# Revit family: Plumbing-Flushometer-Sloan-Valve-ROYAL-115-ESS_
name_source: partatom
category: Plumbing Fixtures
units: mm (PartAtom-declared; Revit-internal decimal feet)

## family parameters
Cut with Voids When Loaded = No
Host = Face
OmniClass Number = 23.45.05.14.99
OmniClass Title = Other Sanitary Washing Plumbing Fixtures
Part Type = Normal
Room Calculation Point = No
Round Connector Dimension = Use Diameter
Shared = No

## types (7) — shared parameters
Apparent Load = 0 VA
Assembly Code = D2020300
CW Connection = Yes
Centerline of Supply from Top of Fixture = 24"
Centerline of Supply to Centerline of Valve = 4 3/4"
Connector Description = Electrical Connection
Current = 0 A
Default Elevation = 0"
Edition number = 1
HW Connection = No
Height = 26 1/2"
Keynote = 15410
Manufacturer = Sloan Valve
Number of Poles = 1
Operating Water Pressure = 15 – 80 PSI (103 – 552 kPa)
Power Factor = 1
Product Material = Sloan Valve - Finish - Polished Chrome
Product data url = https://bimobject.com
URL = www.sloanvalve.com
Valve Pressure Drop = 0.00 psi
Vent Connection = No
Voltage = 24 V
Waste Connection = No
Water Inlet Connection Description = Water Inlet Connection
Water Inlet Connection Diameter = 1"
zero-valued in all types: CWFU, HWFU, WFU

## per-type parameters (varying)
| type | Description | Flush Rate | Part Number | z_2D_2 | z_Distance | z_No OFST | z_OFST | z_Offset | z_Pipe Offset |
| ROYAL 115 ESS-1.6-TMO-HW | 1.6 gpf, Polished Chrome Finish, Fixture Connection Top Spud, Single Flush, True Mechanical Override, Hardwired, Sensor-Operated, Royal® Exposed Sensor Hardwired Water Closet Flushometer. | 1.6 gpf (6.0 Lpf) | 3450310 | No | 2 1/4" | Yes | No | 2 1/4" | 1" |
| ROYAL 115 ESS-1.6-OR-2-OFST-HW | 1.6 gpf, Polished Chrome Finish, Fixture Connection Top Spud, Single Flush, 2 Offset, Electrical Override, Hardwired, Sensor-Operated, Royal® Exposed Sensor Hardwired Water Closet Flushometer. | 1.6 gpf (6.0 Lpf) | 3450348 | Yes | 1 1/4" | No | Yes | 3 1/4" | 2" |
| ROYAL 115 ESS-1.28-TMO-HW | 1.28 gpf, Polished Chrome Finish, Fixture Connection Top Spud, Single Flush, True Mechanical Override, Hardwired, Sensor-Operated, Royal® Exposed Sensor Hardwired Water Closet Flushometer. | 1.28 gpf (4.8 Lpf) | 3450312 | No | 2 1/4" | Yes | No | 2 1/4" | 1" |
| ROYAL 115 ESS-1.6-B-OR-HW | 1.6 gpf, Polished Chrome Finish, Fixture Connection Top Spud, Single Flush, Back of Valve Inlet, Electrical Override, Hardwired, SensorOperated, Royal® Exposed Sensor Hardwired Water Closet Flushometer. | 1.6 gpf (6.0 Lpf) | 3450349 | No | 2 1/4" | Yes | No | 2 1/4" | 1" |
| ROYAL 115 ESS-1.28-OR-HW | 1.28 gpf, Polished Chrome Finish, Fixture Connection Top Spud, Single Flush, Electrical Override, Hardwired, Sensor-Operated, Royal® Exposed Sensor Hardwired Water Closet Flushometer. | 1.28 gpf (4.8 Lpf) | 3450351 | No | 2 1/4" | Yes | No | 2 1/4" | 1" |
| ROYAL 115 ESS-3.5-OR-2-OFST-HW | 3.5 gpf, Polished Chrome Finish, Fixture Connection Top Spud, Single Flush, 2 Offset, Electrical Override, Hardwired, Sensor-Operated, Royal® Exposed Sensor Hardwired Water Closet Flushometer. | 3.5 gpf (13.2 Lpf) | 3450346 | Yes | 1 1/4" | No | Yes | 3 1/4" | 2" |
| ROYAL 115 ESS-3.5-OR-HW | 3.5 gpf, Polished Chrome Finish, Fixture Connection Top Spud, Single Flush, Electrical Override, Hardwired, Sensor-Operated, Royal® Exposed Sensor Hardwired Water Closet Flushometer. | 3.5 gpf (13.2 Lpf) | 3450347 | No | 2 1/4" | Yes | No | 2 1/4" | 1" |

note: column(s) folded — value = type name in every type: Model

## geometry (parser evidence)
native form markers: Sweep x3
no freeform markers — native parametric forms only
